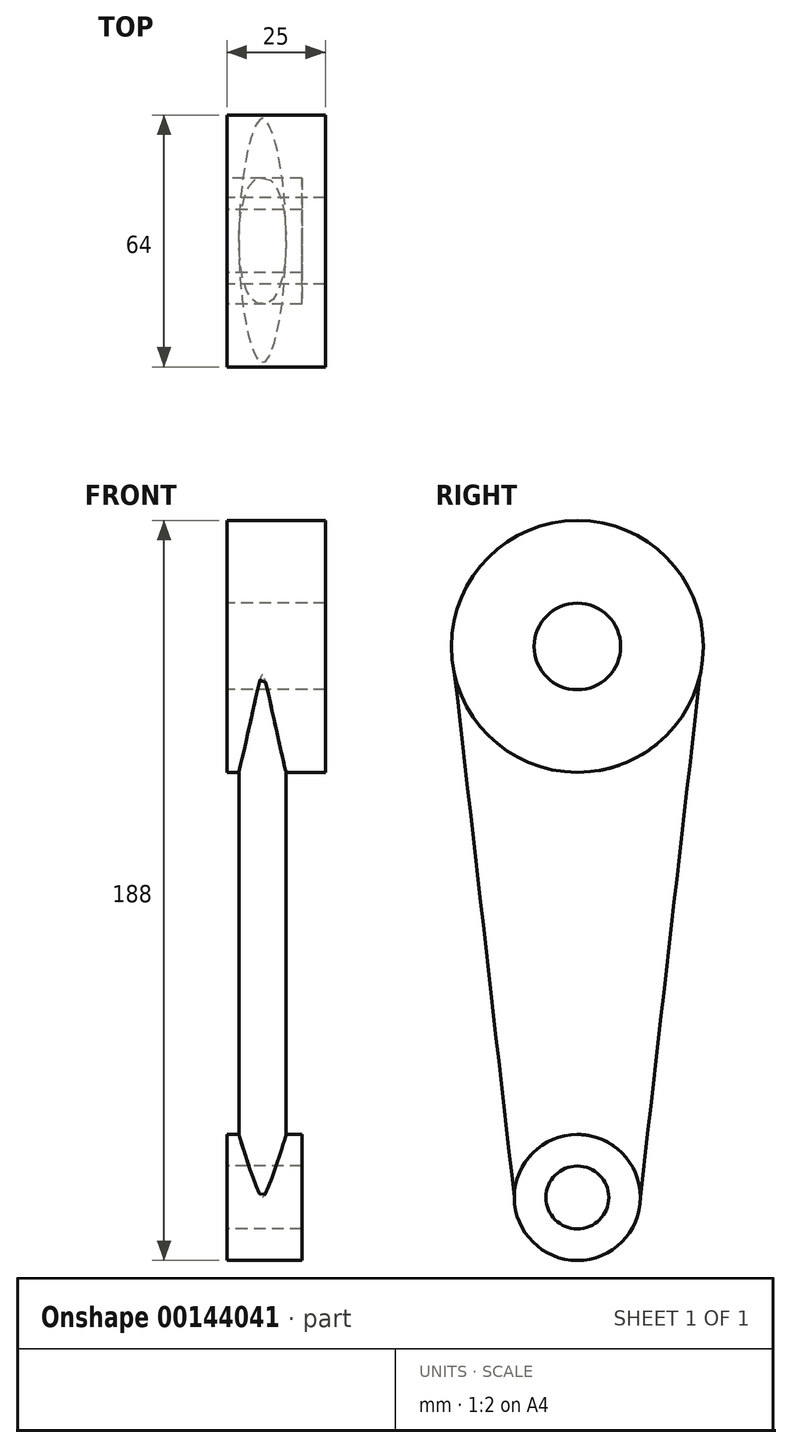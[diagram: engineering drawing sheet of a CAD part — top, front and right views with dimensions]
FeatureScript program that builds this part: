
annotation { "Feature Type Name" : "Feature", "Feature Type Description" : "" }
export const myFeature = defineFeature(function(context is Context, id is Id, definition is map)
    precondition{}
    {
        {
            var Q0;
            Q0=qCreatedBy(makeId("Right.planeOp"),FACE);
            var sketch = newSketch(context, id + "F0", { "sketchPlane" : qUnion([Q0])});
            skCircle(sketch, "E0", {"center": v(0, 0) * mm, "radius": 8 * mm});
            skCircle(sketch, "E1", {"center": v(0, 0) * mm, "radius": 16 * mm});
            skCircle(sketch, "E2", {"center": v(0, 140) * mm, "radius": 11 * mm});
            skCircle(sketch, "E3", {"center": v(0, 140) * mm, "radius": 32 * mm});
            skSolve(sketch);
        }
        {
            var Q0;
            Q0=makeQuery(id+"F0.imprint","IMPRINT",FACE,{"disambiguationData":[TD([[makeQuery(id+"F0.imprint","IMPRINT",EDGE,{"derivedFrom":sQuery(id+"F0.wireOp",EDGE,"E0")}),1.0]])]});
            var Q1;
            Q1=makeQuery(id+"F0.imprint","IMPRINT",FACE,{"disambiguationData":[TD([[makeQuery(id+"F0.imprint","IMPRINT",EDGE,{"derivedFrom":sQuery(id+"F0.wireOp",EDGE,"E0")}),-1.0]])]});
            extrude(context, id + "F1", {"entities" : qUnion([Q0, Q1]), "depth" : 19 * mm});
        }
        {
            var Q0;
            Q0=makeQuery(id+"F0.imprint","IMPRINT",FACE,{"disambiguationData":[TD([[makeQuery(id+"F0.imprint","IMPRINT",EDGE,{"derivedFrom":sQuery(id+"F0.wireOp",EDGE,"E2")}),1.0]])]});
            var Q1;
            Q1=makeQuery(id+"F0.imprint","IMPRINT",FACE,{"disambiguationData":[TD([[makeQuery(id+"F0.imprint","IMPRINT",EDGE,{"derivedFrom":sQuery(id+"F0.wireOp",EDGE,"E2")}),-1.0]])]});
            extrude(context, id + "F2", {"entities" : qUnion([Q0, Q1]), "depth" : 25 * mm});
        }
        {
            var Q0;
            Q0=qCreatedBy(makeId("Top.planeOp"),FACE);
            var sketch = newSketch(context, id + "F3", { "sketchPlane" : qUnion([Q0])});
            skEllipse(sketch, "E4", {"center": v(9, 0) * mm, "majorRadius": 16 * mm, "minorRadius": 6 * mm, "majorAxis": v(0, 1)});
            skPoint(sketch, "E5", {"position": v(3, 0) * mm});
            skLineSegment(sketch, "E6", {"start": v(0, 16) * mm, "end": v(19, 16) * mm, "construction": true});
            skSolve(sketch);
        }
        {
            var Q0;
            Q0=sQuery(id+"F0.wireOp",VERTEX,"E3.center");
            var Q1;
            Q1=qCreatedBy(makeId("Top.planeOp"),FACE);
            cPlane(context, id + "F4", {"entities" : qUnion([Q0, Q1]), "cplaneType" : CPlaneType.PLANE_POINT, "offset" : 25 * mm, "width" : 150 * mm, "height" : 150 * mm});
        }
        {
            var Q0;
            Q0=qCreatedBy(id+"F4.planeOp",FACE);
            var sketch = newSketch(context, id + "F5", { "sketchPlane" : qUnion([Q0])});
            skEllipse(sketch, "E7", {"center": v(9, 0) * mm, "majorRadius": 32 * mm, "minorRadius": 6 * mm, "majorAxis": v(0, 1)});
            skPoint(sketch, "E8", {"position": v(3, 0) * mm});
            skLineSegment(sketch, "E9", {"start": v(0, 32) * mm, "end": v(25, 32) * mm, "construction": true});
            skSolve(sketch);
        }
        {
            var Q0;
            Q0=makeQuery(id+"F5.imprint","IMPRINT",FACE,{"disambiguationData":[TD([[makeQuery(id+"F5.imprint","IMPRINT",EDGE,{"derivedFrom":sQuery(id+"F5.wireOp",EDGE,"E7")}),1.0]])]});
            var Q1;
            Q1=makeQuery(id+"F3.imprint","IMPRINT",FACE,{"disambiguationData":[TD([[makeQuery(id+"F3.imprint","IMPRINT",EDGE,{"derivedFrom":sQuery(id+"F3.wireOp",EDGE,"E4")}),1.0]])]});
            loft(context, id + "F6", {"operationType" : NewBodyOperationType.ADD, "sheetProfilesArray" : [{ "sheetProfileEntities" : qUnion([Q0]) }, { "sheetProfileEntities" : qUnion([Q1]) }]});
        }
        {
            var Q0;
            Q0=makeQuery(id+"F0.imprint","IMPRINT",FACE,{"disambiguationData":[TD([[makeQuery(id+"F0.imprint","IMPRINT",EDGE,{"derivedFrom":sQuery(id+"F0.wireOp",EDGE,"E2")}),1.0]])]});
            var Q1;
            Q1=makeQuery(id+"F0.imprint","IMPRINT",FACE,{"disambiguationData":[TD([[makeQuery(id+"F0.imprint","IMPRINT",EDGE,{"derivedFrom":sQuery(id+"F0.wireOp",EDGE,"E0")}),1.0]])]});
            extrude(context, id + "F7", {"entities" : qUnion([Q0, Q1]), "operationType" : NewBodyOperationType.REMOVE, "depth" : 25 * mm});
        }
    });
